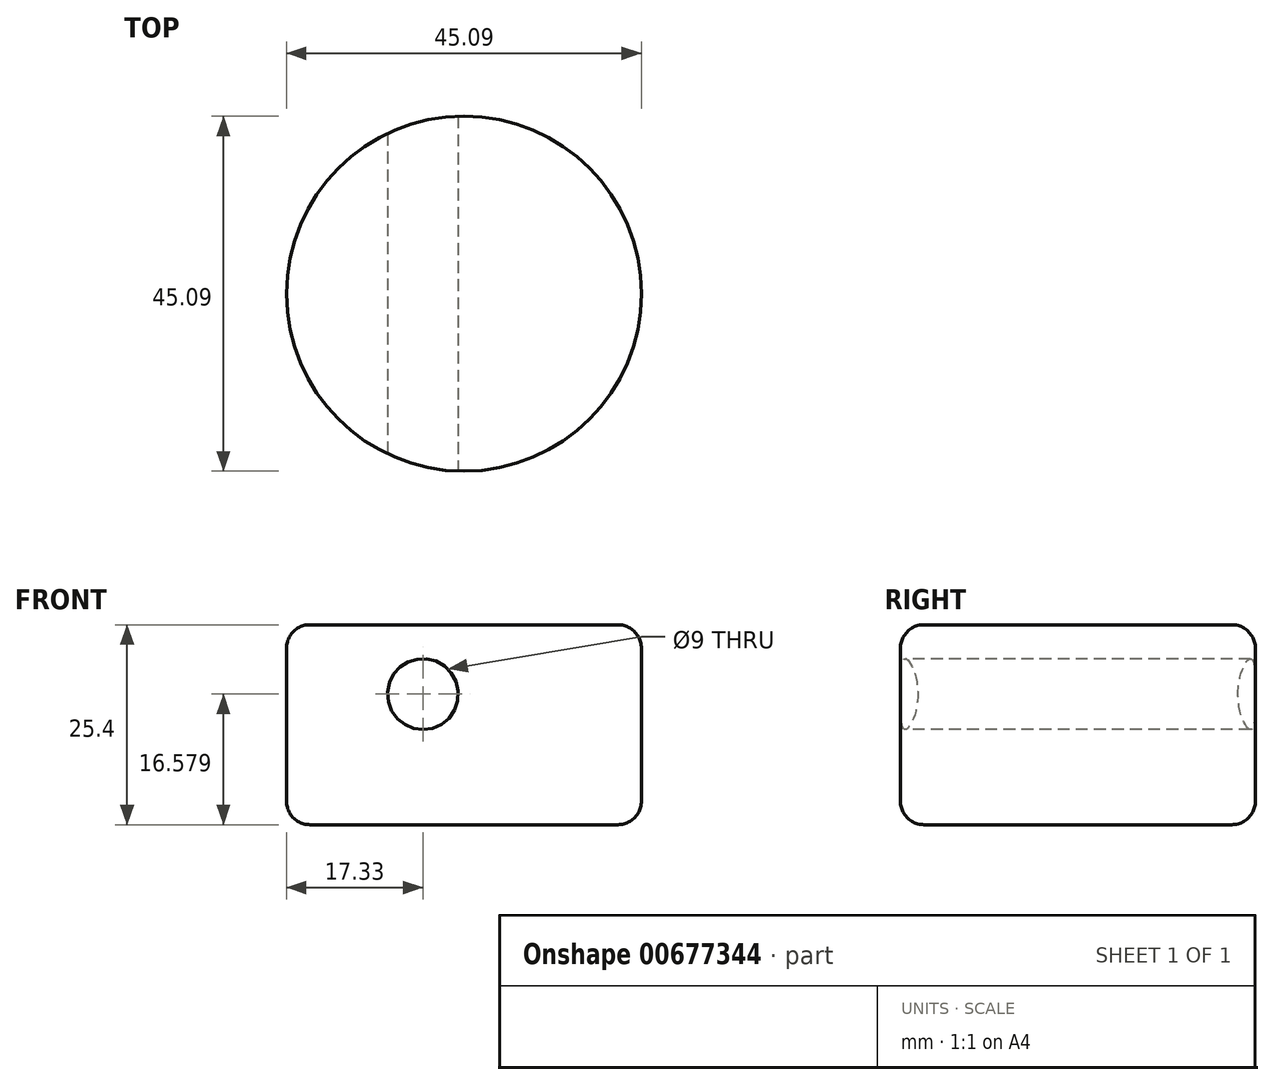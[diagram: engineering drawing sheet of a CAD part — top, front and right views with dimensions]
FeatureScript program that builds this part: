
annotation { "Feature Type Name" : "Feature", "Feature Type Description" : "" }
export const myFeature = defineFeature(function(context is Context, id is Id, definition is map)
    precondition{}
    {
        {
            var Q0;
            Q0=qCreatedBy(makeId("Top.planeOp"),FACE);
            var sketch = newSketch(context, id + "F0", { "sketchPlane" : qUnion([Q0])});
            skCircle(sketch, "E0", {"center": v(-23.6, 23.3) * mm, "radius": 22.55 * mm});
            skSolve(sketch);
        }
        {
            var Q0;
            Q0=makeQuery(id+"F0.imprint","IMPRINT",FACE,{"disambiguationData":[TD([[makeQuery(id+"F0.imprint","IMPRINT",EDGE,{"derivedFrom":sQuery(id+"F0.wireOp",EDGE,"E0")}),1.0]])]});
            extrude(context, id + "F1", {"entities" : qUnion([Q0]), "depth" : 25.4 * mm, "offsetDistance" : 25.4 * mm});
        }
        {
            var Q0;
            Q0=qCreatedBy(makeId("Front.planeOp"),FACE);
            var sketch = newSketch(context, id + "F2", { "sketchPlane" : qUnion([Q0])});
            skCircle(sketch, "E1", {"center": v(-28.82, 16.58) * mm, "radius": 4.5 * mm});
            skSolve(sketch);
        }
        {
            var Q0;
            Q0=sQuery(id+"F2.wireOp",VERTEX,"E1.center");
            var Q1;
            Q1=makeQuery(id+"F1.opExtrude","SWEPT_BODY",BODY,{"disambiguationData":[OSD([sQuery(id+"F0.wireOp",EDGE,"E0")])]});
            hole(context, id + "F3", {"style" : HoleStyle.SIMPLE, "endStyle" : HoleEndStyle.THROUGH, "holeDiameter" : 9 * mm, "majorDiameter" : 5 * mm, "isTappedThrough" : true, "tappedDepth" : 12 * mm, "tapClearance" : 3, "locations" : qUnion([Q0]), "scope" : qUnion([Q1])});
        }
        {
            var Q0;
            Q0=makeQuery(id+"F1.opExtrude","CAP_EDGE",EDGE,{"disambiguationData":[OSD([sQuery(id+"F0.wireOp",EDGE,"E0")])],"isStart":false});
            var Q1;
            Q1=makeQuery(id+"F1.opExtrude","CAP_EDGE",EDGE,{"disambiguationData":[OSD([sQuery(id+"F0.wireOp",EDGE,"E0")])],"isStart":true});
            fillet(context, id + "F4", {"entities" : qUnion([Q0, Q1]), "radius" : 3 * mm, "tangentPropagation" : true, "allowEdgeOverflow" : false});
        }
    });
